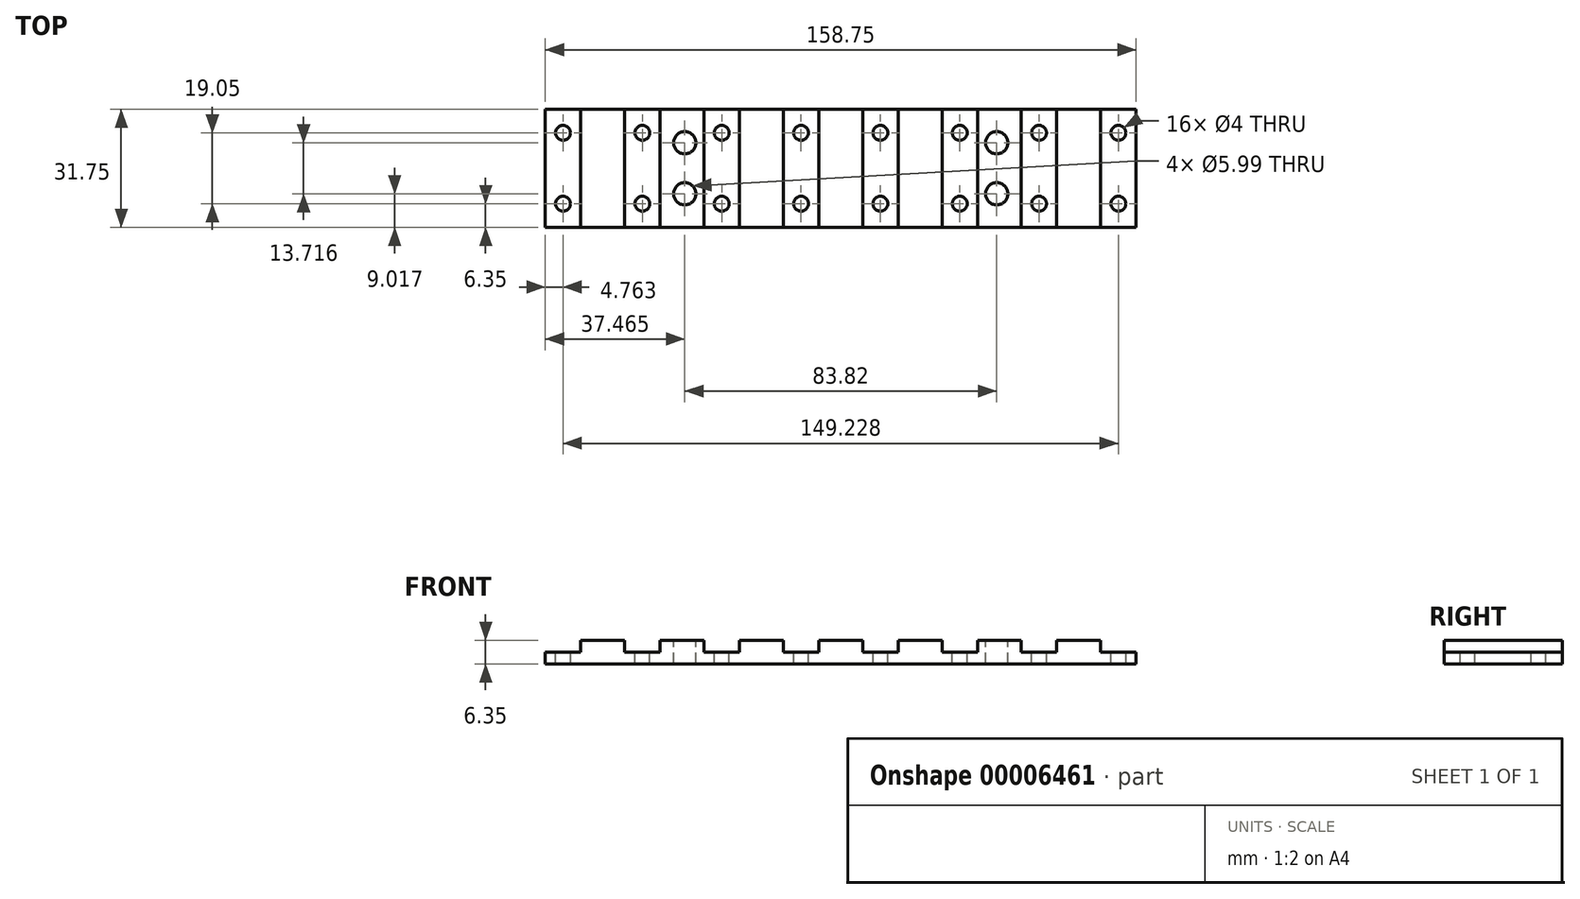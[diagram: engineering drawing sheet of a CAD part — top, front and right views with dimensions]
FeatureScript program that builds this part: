
annotation { "Feature Type Name" : "Feature", "Feature Type Description" : "" }
export const myFeature = defineFeature(function(context is Context, id is Id, definition is map)
    precondition{}
    {
        {
            var Q0;
            Q0=qCreatedBy(makeId("Top.planeOp"),FACE);
            var sketch = newSketch(context, id + "F0", { "sketchPlane" : qUnion([Q0])});
            skLineSegment(sketch, "E0.bottom", {"start": v(0, 0) * mm, "end": v(158.75, 0) * mm});
            skLineSegment(sketch, "E0.top", {"start": v(0, -31.75) * mm, "end": v(158.75, -31.75) * mm});
            skLineSegment(sketch, "E0.left", {"start": v(0, 0) * mm, "end": v(0, -31.75) * mm});
            skLineSegment(sketch, "E0.right", {"start": v(158.75, 0) * mm, "end": v(158.75, -31.75) * mm});
            skSolve(sketch);
        }
        {
            var Q0;
            Q0 = qSketchRegion(id + "F0", true);
            extrude(context, id + "F1", {"entities" : qUnion([Q0]), "depth" : 6.35 * mm});
        }
        {
            var Q0;
            Q0=makeQuery(id+"F1.opExtrude","CAP_FACE",FACE,{"disambiguationData":[OSD([sQuery(id+"F0.wireOp",EDGE,"E0.bottom"),sQuery(id+"F0.wireOp",EDGE,"E0.top"),sQuery(id+"F0.wireOp",EDGE,"E0.left"),sQuery(id+"F0.wireOp",EDGE,"E0.right")])],"isStart":false});
            var sketch = newSketch(context, id + "F2", { "sketchPlane" : qUnion([Q0])});
            skLineSegment(sketch, "E1.bottom", {"start": v(37.46, -9.02) * mm, "end": v(121.29, -9.02) * mm, "construction": true});
            skLineSegment(sketch, "E1.top", {"start": v(37.46, -22.73) * mm, "end": v(121.29, -22.73) * mm, "construction": true});
            skLineSegment(sketch, "E1.left", {"start": v(37.46, -9.02) * mm, "end": v(37.46, -22.73) * mm, "construction": true});
            skLineSegment(sketch, "E1.right", {"start": v(121.29, -9.02) * mm, "end": v(121.29, -22.73) * mm, "construction": true});
            skCircle(sketch, "E2", {"center": v(37.46, -9.02) * mm, "radius": 3 * mm});
            skCircle(sketch, "E3", {"center": v(37.46, -22.73) * mm, "radius": 3 * mm});
            skCircle(sketch, "E4", {"center": v(121.29, -22.73) * mm, "radius": 3 * mm});
            skCircle(sketch, "E5", {"center": v(121.29, -9.02) * mm, "radius": 3 * mm});
            skLineSegment(sketch, "E6", {"start": v(79.38, 0) * mm, "end": v(79.38, -9.02) * mm, "construction": true});
            skLineSegment(sketch, "E7", {"start": v(37.46, -15.87) * mm, "end": v(0, -15.88) * mm, "construction": true});
            skSolve(sketch);
        }
        {
            var Q0;
            Q0 = qSketchRegion(id + "F2", true);
            extrude(context, id + "F3", {"entities" : qUnion([Q0]), "operationType" : NewBodyOperationType.REMOVE, "endBound" : BoundingType.THROUGH_ALL, "oppositeDirection" : true, "depth" : 25.4 * mm});
        }
        {
            var Q0;
            Q0=makeQuery(id+"F1.opExtrude","CAP_FACE",FACE,{"disambiguationData":[OSD([sQuery(id+"F0.wireOp",EDGE,"E0.bottom"),sQuery(id+"F0.wireOp",EDGE,"E0.top"),sQuery(id+"F0.wireOp",EDGE,"E0.left"),sQuery(id+"F0.wireOp",EDGE,"E0.right")])],"isStart":false});
            var sketch = newSketch(context, id + "F4", { "sketchPlane" : qUnion([Q0])});
            skLineSegment(sketch, "E8.bottom", {"start": v(0, 0) * mm, "end": v(9.53, 0) * mm});
            skLineSegment(sketch, "E8.top", {"start": v(0, -31.75) * mm, "end": v(9.53, -31.75) * mm});
            skLineSegment(sketch, "E8.left", {"start": v(0, 0) * mm, "end": v(0, -31.75) * mm});
            skLineSegment(sketch, "E8.right", {"start": v(9.53, 0) * mm, "end": v(9.53, -31.75) * mm});
            skLineSegment(sketch, "E9.1.0.1", {"start": v(21.32, 0) * mm, "end": v(30.84, 0) * mm});
            skLineSegment(sketch, "E9.1.0.2", {"start": v(21.32, -31.75) * mm, "end": v(30.84, -31.75) * mm});
            skLineSegment(sketch, "E9.1.0.5", {"start": v(21.32, 0) * mm, "end": v(21.32, -31.75) * mm});
            skLineSegment(sketch, "E9.1.0.7", {"start": v(30.84, 0) * mm, "end": v(30.84, -31.75) * mm});
            skLineSegment(sketch, "E9.2.0.1", {"start": v(42.64, 0) * mm, "end": v(52.16, 0) * mm});
            skLineSegment(sketch, "E9.2.0.2", {"start": v(42.64, -31.75) * mm, "end": v(52.16, -31.75) * mm});
            skLineSegment(sketch, "E9.2.0.5", {"start": v(42.64, 0) * mm, "end": v(42.64, -31.75) * mm});
            skLineSegment(sketch, "E9.2.0.7", {"start": v(52.16, 0) * mm, "end": v(52.16, -31.75) * mm});
            skLineSegment(sketch, "E9.3.0.1", {"start": v(63.95, 0) * mm, "end": v(73.48, 0) * mm});
            skLineSegment(sketch, "E9.3.0.2", {"start": v(63.95, -31.75) * mm, "end": v(73.48, -31.75) * mm});
            skLineSegment(sketch, "E9.3.0.5", {"start": v(63.95, 0) * mm, "end": v(63.95, -31.75) * mm});
            skLineSegment(sketch, "E9.3.0.7", {"start": v(73.48, 0) * mm, "end": v(73.48, -31.75) * mm});
            skLineSegment(sketch, "E9.4.0.1", {"start": v(85.27, 0) * mm, "end": v(94.8, 0) * mm});
            skLineSegment(sketch, "E9.4.0.2", {"start": v(85.27, -31.75) * mm, "end": v(94.8, -31.75) * mm});
            skLineSegment(sketch, "E9.4.0.5", {"start": v(85.27, 0) * mm, "end": v(85.27, -31.75) * mm});
            skLineSegment(sketch, "E9.4.0.7", {"start": v(94.8, 0) * mm, "end": v(94.8, -31.75) * mm});
            skLineSegment(sketch, "E9.5.0.1", {"start": v(106.59, 0) * mm, "end": v(116.11, 0) * mm});
            skLineSegment(sketch, "E9.5.0.2", {"start": v(106.59, -31.75) * mm, "end": v(116.11, -31.75) * mm});
            skLineSegment(sketch, "E9.5.0.5", {"start": v(106.59, 0) * mm, "end": v(106.59, -31.75) * mm});
            skLineSegment(sketch, "E9.5.0.7", {"start": v(116.11, 0) * mm, "end": v(116.11, -31.75) * mm});
            skLineSegment(sketch, "E9.6.0.1", {"start": v(127.9, 0) * mm, "end": v(137.43, 0) * mm});
            skLineSegment(sketch, "E9.6.0.2", {"start": v(127.9, -31.75) * mm, "end": v(137.43, -31.75) * mm});
            skLineSegment(sketch, "E9.6.0.5", {"start": v(127.9, 0) * mm, "end": v(127.9, -31.75) * mm});
            skLineSegment(sketch, "E9.6.0.7", {"start": v(137.43, 0) * mm, "end": v(137.43, -31.75) * mm});
            skLineSegment(sketch, "E9.7.0.1", {"start": v(149.22, 0) * mm, "end": v(158.75, 0) * mm});
            skLineSegment(sketch, "E9.7.0.2", {"start": v(149.22, -31.75) * mm, "end": v(158.75, -31.75) * mm});
            skLineSegment(sketch, "E9.7.0.5", {"start": v(149.22, 0) * mm, "end": v(149.22, -31.75) * mm});
            skLineSegment(sketch, "E9.7.0.7", {"start": v(158.75, 0) * mm, "end": v(158.75, -31.75) * mm});
            skLineSegment(sketch, "E9.direction1", {"start": v(9.53, -31.75) * mm, "end": v(33.53, -31.75) * mm, "construction": true});
            skSolve(sketch);
        }
        {
            var Q0;
            Q0 = qSketchRegion(id + "F4", true);
            extrude(context, id + "F5", {"entities" : qUnion([Q0]), "operationType" : NewBodyOperationType.REMOVE, "oppositeDirection" : true, "depth" : 3.17 * mm});
        }
        {
            var Q0;
            Q0=makeQuery(id+"F5.boolean.opBoolean","COPY",FACE,{"derivedFrom":makeQuery(id+"F5.opExtrude","CAP_FACE",FACE,{"disambiguationData":[OSD([sQuery(id+"F4.wireOp",EDGE,"E8.bottom"),sQuery(id+"F4.wireOp",EDGE,"E8.top"),sQuery(id+"F4.wireOp",EDGE,"E8.left"),sQuery(id+"F4.wireOp",EDGE,"E8.right")])],"isStart":false})});
            var sketch = newSketch(context, id + "F6", { "sketchPlane" : qUnion([Q0])});
            skCircle(sketch, "E10", {"center": v(4.76, -6.35) * mm, "radius": 2 * mm});
            skCircle(sketch, "E11", {"center": v(4.76, -25.4) * mm, "radius": 2 * mm});
            skLineSegment(sketch, "E12", {"start": v(4.76, -6.35) * mm, "end": v(4.76, 0) * mm, "construction": true});
            skLineSegment(sketch, "E13", {"start": v(4.76, -25.4) * mm, "end": v(4.76, -31.75) * mm, "construction": true});
            skCircle(sketch, "E14.1.0.0", {"center": v(26.08, -25.4) * mm, "radius": 2 * mm});
            skLineSegment(sketch, "E14.1.0.1", {"start": v(26.08, -25.4) * mm, "end": v(26.08, -31.75) * mm, "construction": true});
            skCircle(sketch, "E14.1.0.2", {"center": v(26.08, -6.35) * mm, "radius": 2 * mm});
            skLineSegment(sketch, "E14.1.0.3", {"start": v(26.08, -6.35) * mm, "end": v(26.08, 0) * mm, "construction": true});
            skCircle(sketch, "E14.2.0.0", {"center": v(47.4, -25.4) * mm, "radius": 2 * mm});
            skLineSegment(sketch, "E14.2.0.1", {"start": v(47.4, -25.4) * mm, "end": v(47.4, -31.75) * mm, "construction": true});
            skCircle(sketch, "E14.2.0.2", {"center": v(47.4, -6.35) * mm, "radius": 2 * mm});
            skLineSegment(sketch, "E14.2.0.3", {"start": v(47.4, -6.35) * mm, "end": v(47.4, 0) * mm, "construction": true});
            skCircle(sketch, "E14.3.0.0", {"center": v(68.72, -25.4) * mm, "radius": 2 * mm});
            skLineSegment(sketch, "E14.3.0.1", {"start": v(68.72, -25.4) * mm, "end": v(68.72, -31.75) * mm, "construction": true});
            skCircle(sketch, "E14.3.0.2", {"center": v(68.72, -6.35) * mm, "radius": 2 * mm});
            skLineSegment(sketch, "E14.3.0.3", {"start": v(68.72, -6.35) * mm, "end": v(68.72, 0) * mm, "construction": true});
            skCircle(sketch, "E14.4.0.0", {"center": v(90.04, -25.4) * mm, "radius": 2 * mm});
            skLineSegment(sketch, "E14.4.0.1", {"start": v(90.04, -25.4) * mm, "end": v(90.04, -31.75) * mm, "construction": true});
            skCircle(sketch, "E14.4.0.2", {"center": v(90.04, -6.35) * mm, "radius": 2 * mm});
            skLineSegment(sketch, "E14.4.0.3", {"start": v(90.04, -6.35) * mm, "end": v(90.04, 0) * mm, "construction": true});
            skCircle(sketch, "E14.5.0.0", {"center": v(111.35, -25.4) * mm, "radius": 2 * mm});
            skLineSegment(sketch, "E14.5.0.1", {"start": v(111.35, -25.4) * mm, "end": v(111.35, -31.75) * mm, "construction": true});
            skCircle(sketch, "E14.5.0.2", {"center": v(111.35, -6.35) * mm, "radius": 2 * mm});
            skLineSegment(sketch, "E14.5.0.3", {"start": v(111.35, -6.35) * mm, "end": v(111.35, 0) * mm, "construction": true});
            skCircle(sketch, "E14.6.0.0", {"center": v(132.67, -25.4) * mm, "radius": 2 * mm});
            skLineSegment(sketch, "E14.6.0.1", {"start": v(132.67, -25.4) * mm, "end": v(132.67, -31.75) * mm, "construction": true});
            skCircle(sketch, "E14.6.0.2", {"center": v(132.67, -6.35) * mm, "radius": 2 * mm});
            skLineSegment(sketch, "E14.6.0.3", {"start": v(132.67, -6.35) * mm, "end": v(132.67, 0) * mm, "construction": true});
            skCircle(sketch, "E14.7.0.0", {"center": v(154, -25.4) * mm, "radius": 2 * mm});
            skLineSegment(sketch, "E14.7.0.1", {"start": v(154, -25.4) * mm, "end": v(154, -31.75) * mm, "construction": true});
            skCircle(sketch, "E14.7.0.2", {"center": v(154, -6.35) * mm, "radius": 2 * mm});
            skLineSegment(sketch, "E14.7.0.3", {"start": v(154, -6.35) * mm, "end": v(154, 0) * mm, "construction": true});
            skLineSegment(sketch, "E14.direction1", {"start": v(4.76, -25.4) * mm, "end": v(26.08, -25.4) * mm, "construction": true});
            skSolve(sketch);
        }
        {
            var Q0;
            Q0 = qSketchRegion(id + "F6", true);
            extrude(context, id + "F7", {"entities" : qUnion([Q0]), "operationType" : NewBodyOperationType.REMOVE, "endBound" : BoundingType.THROUGH_ALL, "oppositeDirection" : true, "depth" : 25.4 * mm});
        }
    });
